# Revit family: PRD_FrankeWS_WlHngWshBsns_AnimaWashbasin_WT400C,WT400C-M
name_source: partatom
category: Plumbing Fixtures
revit_build: Autodesk Revit 2018 (Build: 20190510_1515(x64)
units: mm (PartAtom-declared; Revit-internal decimal feet)

## family parameters
Cut with Voids When Loaded = No
Host = Face
OmniClass Number = 23.45.05.14.14
OmniClass Title = Sinks/Lavatories
Part Type = Normal
Room Calculation Point = No
Round Connector Dimension = Use Diameter
Shared = No

## types (2) — shared parameters
AssetType = Fixed
Category = Pr_40_20_96_96, Wall-hung wash basins
Default Elevation = 850 mm  [stored 2.78871 ft]
DrainSize = DN 32 (1 1/4 inch.)
DurationUnit = year
Features = stainless steel, 1.00 mm, satin finished, wall mounting, 400x150x452 mm (WxHxD)
Form = Wall hung wash basin
IfcExportAs = IfcSanitaryTerminalType
IfcExportType = WASHHANDBASIN
Manufacturer = KWC Group AG
ManufacturerName = KWC Group AG
ManufacturerURL = www.kwc.com
NBSDescription = Wall hung wash basins
NBSReference = 45-35-70/369
NominalDepth = 452 mm  [stored 1.48294 ft]
NominalHeight = 150 mm
NominalWidth = 400 mm  [stored 1.31234 ft]
OutletSize = DN 32 (1 1/4 inch.)
Overflow = yes
OverflowLocation = Back
ProductInformation = https://pim.kwc.com
Shape = Rectangular
SinkMounting = WallHung
SinkType = HandRinse
Size = 400 x 452 x 150 mm
SplashbackMaterial = PRD_AR_StainlessSteel_SatinFinished
TapLedge = yes
TypeOfMounting = Wall mounting
TypeOfWasteKit = plug waste
URL = www.kwc.com
Uniclass2015Code = Pr_40_20_96_96
Uniclass2015Title = Wall-hung wash basins
Uniclass2015Version = Products v1.10
Version = 1
WarrantyDurationUnit = year
WashbasinMaterial = PRD_AR_StainlessSteel_SatinFinished
WasteHolePosition = Center-Back
WasteSize = 32  [stored 0.104987 ft]

## per-type parameters (varying)
| type | BIMObjectName | Color | Description | Finish | GrossWeight | IntegralAccessories | Material | MaterialCode | ModelNumber | Name | NetWeight | Taphole |
| WT400C-M | PRD_AR_WallHungWashBasins_AnimaWashbasin_WT400C-M | Stainless steel | Single wash basin for wall mounting, stainless steel, surface satin finished, material thickness 1 mm, seamless welded bowl with diameter 340x305x140 mm, rectangular shape, 120 mm tap ledge, with overflow, 1 1/4 plug waste, drainage rewards centric, front panel with 45° corner edges, prewelded mounting brackets, mounting conform EN 31, incl. screws and dowels. Overflow options-7 = no overflow-8 = with overflow with taphole | Satin finished | 4.20 kg | Incl. stainless steel screws and dowels | Stainless steel | Stainless steel 1.4301 | 2000103763 | ANIMA wall-hung wash basin WT400C-M | 4.00 kg | Yes |
| WT400C | PRD_AR_WallHungWashBasins_AnimaWashbasin_WT400C | stainless steel | Single wash basin for wall mounting, stainless steel, surface satin finished, material thickness 1 mm, seamless welded bowl with diameter 340x305x140 mm, rectangular shape, 120 mm tap ledge, with overflow, 1 1/4 plug waste, drainage rewards centric, front panel with 45° corner edges, prewelded mounting brackets, mounting conform EN 31, incl. screws and dowels. Overflow options-7 = no overflow-8 = with overflow | satin finished | 3.44 kg | Incl. screws and dowels | stainless steel | stainless steel 1.4301 | 2000090020 | Anima wall-hung wash basins WT400C | 3.20 kg | No |

note: column(s) folded — value = type name in every type: Model, ModelReference, Type

note: [stored X ft] marks values corroborated as IEEE doubles in the binary element streams (Revit-internal decimal feet)

## geometry (parser evidence)
native form markers: Sweep x9
no freeform markers — native parametric forms only
